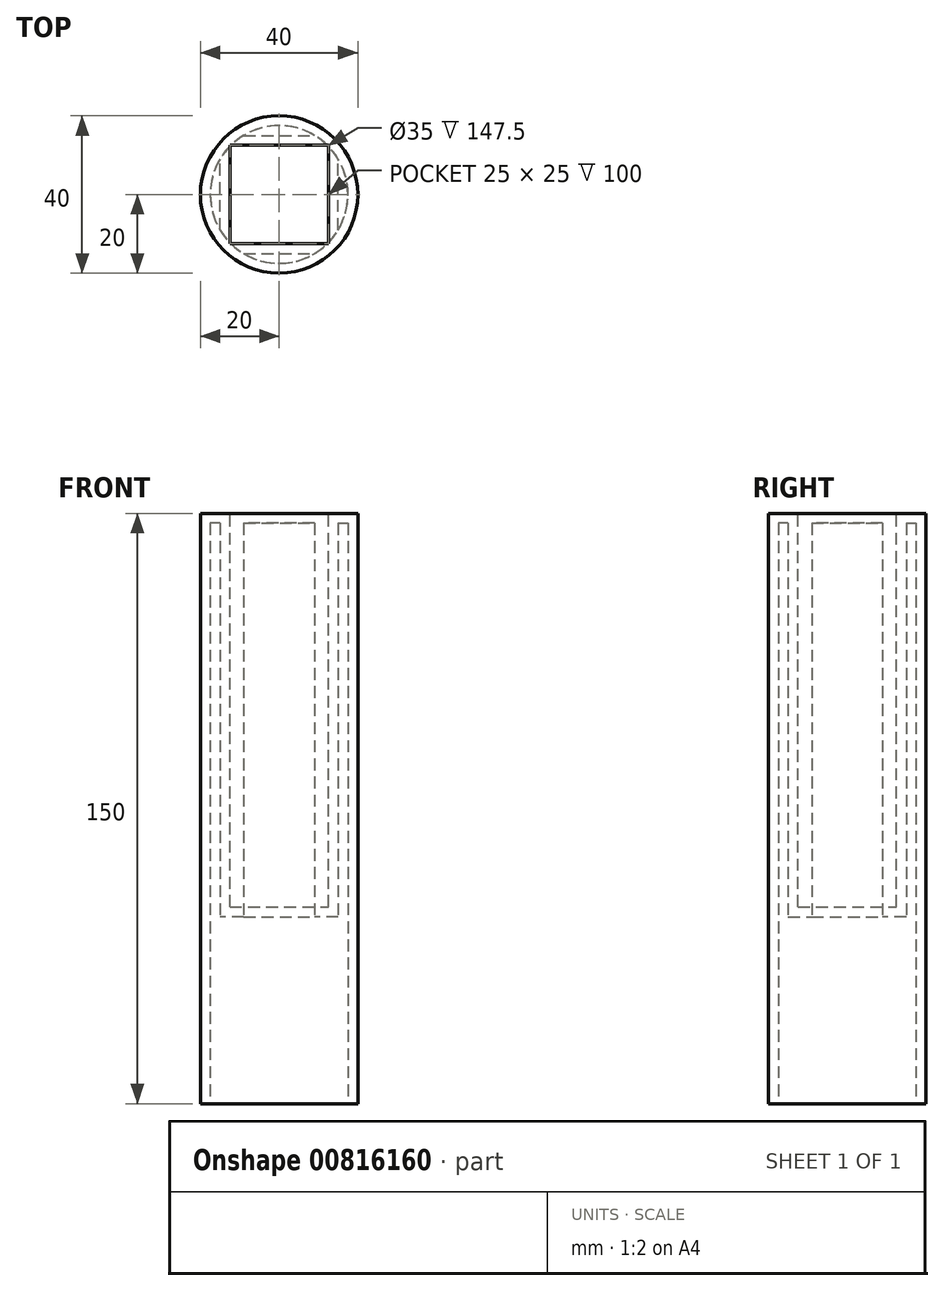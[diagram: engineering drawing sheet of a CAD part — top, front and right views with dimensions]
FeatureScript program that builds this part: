
annotation { "Feature Type Name" : "Feature", "Feature Type Description" : "" }
export const myFeature = defineFeature(function(context is Context, id is Id, definition is map)
    precondition{}
    {
        {
            var Q0;
            Q0=qCreatedBy(makeId("Top.planeOp"),FACE);
            var sketch = newSketch(context, id + "F0", { "sketchPlane" : qUnion([Q0])});
            skCircle(sketch, "E0", {"center": v(0, 0) * mm, "radius": 20 * mm});
            skCircle(sketch, "E1", {"center": v(0, 0) * mm, "radius": 7.5 * mm});
            skSolve(sketch);
        }
        {
            var Q0;
            Q0 = qSketchRegion(id + "F0", true);
            var Q1;
            Q1=makeQuery(id+"F0.imprint","IMPRINT",FACE,{"disambiguationData":[TD([[makeQuery(id+"F0.imprint","IMPRINT",EDGE,{"derivedFrom":sQuery(id+"F0.wireOp",EDGE,"E1")}),1.0]])]});
            extrude(context, id + "F1", {"entities" : qUnion([Q0, Q1]), "depth" : 150 * mm, "offsetDistance" : 25 * mm});
        }
        {
            var Q0;
            Q0=makeQuery(id+"F1.opExtrude","CAP_FACE",FACE,{"disambiguationData":[OSD([sQuery(id+"F0.wireOp",EDGE,"E0")])],"isStart":false});
            var sketch = newSketch(context, id + "F2", { "sketchPlane" : qUnion([Q0])});
            skLineSegment(sketch, "E2.bottom", {"start": v(-12.5, -12.5) * mm, "end": v(12.5, -12.5) * mm});
            skLineSegment(sketch, "E2.top", {"start": v(-12.5, 12.5) * mm, "end": v(12.5, 12.5) * mm});
            skLineSegment(sketch, "E2.left", {"start": v(-12.5, -12.5) * mm, "end": v(-12.5, 12.5) * mm});
            skLineSegment(sketch, "E2.right", {"start": v(12.5, -12.5) * mm, "end": v(12.5, 12.5) * mm});
            skPoint(sketch, "E2.middle", {"position": v(0, 0) * mm});
            skSolve(sketch);
        }
        {
            var Q0;
            Q0=makeQuery(id+"F2.imprint","IMPRINT",FACE,{"disambiguationData":[TD([[makeQuery(id+"F2.imprint","IMPRINT",EDGE,{"derivedFrom":sQuery(id+"F2.wireOp",EDGE,"y1hzRh7T-q5qX-rySO-fx97-kLiP26W2DwMy")}),1.0]])]});
            var Q1;
            Q1=makeQuery(id+"F2.imprint","IMPRINT",FACE,{"disambiguationData":[TD([[makeQuery(id+"F2.imprint","IMPRINT",EDGE,{"derivedFrom":sQuery(id+"F2.wireOp",EDGE,"E2.bottom")}),1.0]])]});
            extrude(context, id + "F3", {"entities" : qUnion([Q0, Q1]), "operationType" : NewBodyOperationType.REMOVE, "oppositeDirection" : true, "depth" : 100 * mm, "offsetDistance" : 25 * mm});
        }
        {
            var Q0;
            Q0=makeQuery(id+"F1.opExtrude","CAP_FACE",FACE,{"disambiguationData":[OSD([sQuery(id+"F0.wireOp",EDGE,"E0")])],"isStart":true});
            shell(context, id + "F4", {"entities" : qUnion([Q0]), "thickness" : 2.5 * mm});
        }
    });
